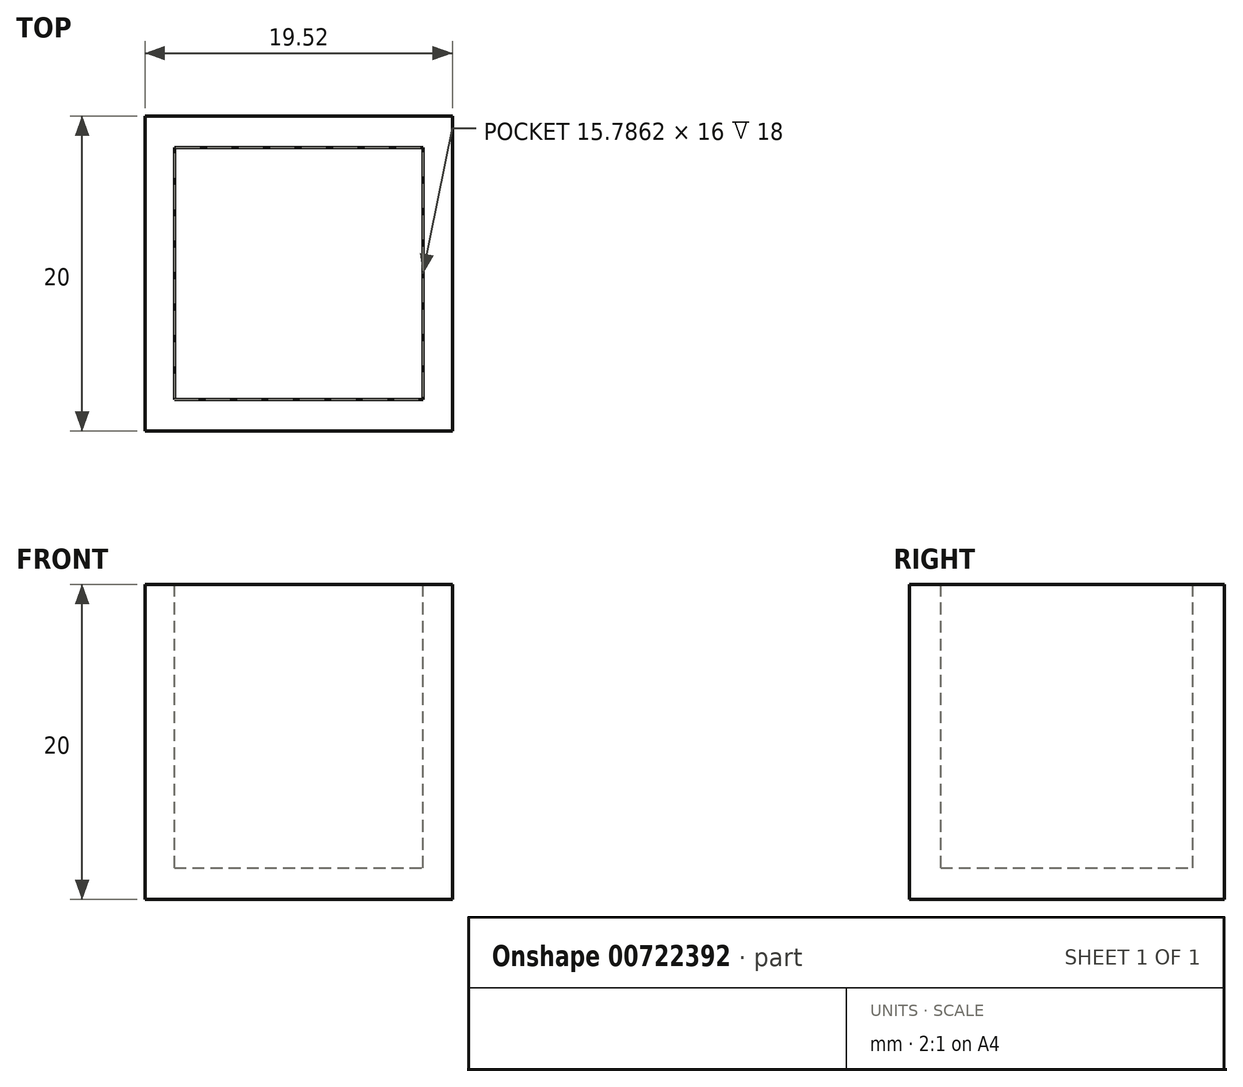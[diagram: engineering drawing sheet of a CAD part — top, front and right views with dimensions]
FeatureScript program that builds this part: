
annotation { "Feature Type Name" : "Feature", "Feature Type Description" : "" }
export const myFeature = defineFeature(function(context is Context, id is Id, definition is map)
    precondition{}
    {
        {
            var Q0;
            Q0=qCreatedBy(makeId("Top.planeOp"),FACE);
            var sketch = newSketch(context, id + "F0", { "sketchPlane" : qUnion([Q0])});
            skLineSegment(sketch, "E0.bottom", {"start": v(0, 0) * mm, "end": v(9.76, 0) * mm});
            skLineSegment(sketch, "E0.top", {"start": v(0, -10) * mm, "end": v(9.76, -10) * mm});
            skLineSegment(sketch, "E0.left", {"start": v(0, 0) * mm, "end": v(0, -10) * mm});
            skLineSegment(sketch, "E0.right", {"start": v(9.76, 0) * mm, "end": v(9.76, -10) * mm});
            skLineSegment(sketch, "E1.MirrorCS", {"start": v(9.76, 0) * mm, "end": v(9.76, 10) * mm});
            skLineSegment(sketch, "E2.MirrorCS", {"start": v(0, 0) * mm, "end": v(0, 10) * mm});
            skLineSegment(sketch, "E3.MirrorCS", {"start": v(0, 10) * mm, "end": v(9.76, 10) * mm});
            skLineSegment(sketch, "E4.MirrorCS", {"start": v(0, 0) * mm, "end": v(-9.76, 0) * mm});
            skLineSegment(sketch, "E5.MirrorCS", {"start": v(0, 10) * mm, "end": v(-9.76, 10) * mm});
            skLineSegment(sketch, "E6.MirrorCS", {"start": v(0, -10) * mm, "end": v(-9.76, -10) * mm});
            skLineSegment(sketch, "E7.MirrorCS", {"start": v(-9.76, 0) * mm, "end": v(-9.76, -10) * mm});
            skLineSegment(sketch, "E8.MirrorCS", {"start": v(-9.76, 0) * mm, "end": v(-9.76, 10) * mm});
            skSolve(sketch);
        }
        {
            var Q0;
            Q0 = qSketchRegion(id + "F0", true);
            extrude(context, id + "F1", {"entities" : qUnion([Q0]), "depth" : 20 * mm, "offsetDistance" : 25 * mm});
        }
        {
            var Q0;
            Q0=makeQuery(id+"F1.opExtrude","CAP_FACE",FACE,{"disambiguationData":[OSD([sQuery(id+"F0.wireOp",EDGE,"E0.top"),sQuery(id+"F0.wireOp",EDGE,"E0.right"),sQuery(id+"F0.wireOp",EDGE,"E1.MirrorCS"),sQuery(id+"F0.wireOp",EDGE,"E3.MirrorCS"),sQuery(id+"F0.wireOp",EDGE,"E5.MirrorCS"),sQuery(id+"F0.wireOp",EDGE,"E6.MirrorCS"),sQuery(id+"F0.wireOp",EDGE,"E7.MirrorCS"),sQuery(id+"F0.wireOp",EDGE,"E8.MirrorCS")])],"isStart":false});
            var sketch = newSketch(context, id + "F2", { "sketchPlane" : qUnion([Q0])});
            skLineSegment(sketch, "E9.top", {"start": v(0, 8) * mm, "end": v(-7.9, 8) * mm});
            skLineSegment(sketch, "E9.right", {"start": v(-7.9, 0) * mm, "end": v(-7.9, 8) * mm});
            skLineSegment(sketch, "E10.right", {"start": v(7.9, 0) * mm, "end": v(7.9, -8) * mm});
            skLineSegment(sketch, "E11.bottom", {"start": v(-7.9, 8) * mm, "end": v(7.9, 8) * mm});
            skLineSegment(sketch, "E11.top", {"start": v(-7.9, -8) * mm, "end": v(7.9, -8) * mm});
            skLineSegment(sketch, "E11.left", {"start": v(-7.9, 8) * mm, "end": v(-7.9, -8) * mm});
            skLineSegment(sketch, "E11.right", {"start": v(7.9, 8) * mm, "end": v(7.9, -8) * mm});
            skSolve(sketch);
        }
        {
            var Q0;
            Q0 = qSketchRegion(id + "F2", true);
            extrude(context, id + "F3", {"entities" : qUnion([Q0]), "operationType" : NewBodyOperationType.REMOVE, "oppositeDirection" : true, "depth" : 18 * mm, "offsetDistance" : 25 * mm});
        }
    });
